# Revit family: EZTE-ELECTRIC ENCL BTM
name_source: partatom
category: Mechanical Equipment
revit_build: Autodesk Revit 2018 (Build: 20170223_1515(x64)
units: mm (PartAtom-declared; Revit-internal decimal feet)

## family parameters
Always vertical = Yes
Cut with Voids When Loaded = No
OmniClass Number = 23.75.00.00
OmniClass Title = Climate Control (HVAC)
Part Type = Normal
Room Calculation Point = No
Round Connector Dimension = Use Diameter
Shared = No
Work Plane-Based = No

## types (9) — shared parameters
Discharge = 0' - 0 5/8"
EZTE Length = 3' - 3 1/2"
EZTE Rear Side = 3' - 2 7/8"
Electric Encl Length = 2' - 0"
Electric Encl distance from discharge = 0' - 2 1/8"
Enclosure Distance from Front = 0' - 4"
Enclosure Height = 0' - 11 3/32"
Enclosure Length = 1' - 2 7/32"
Enclosure Optional = Yes
Inlet Distance S = 0' - 5 3/8"
Width = 0' - 7 1/4"

## per-type parameters (varying)
| type | Between Encl and Electric | DisCharge Height | DisCharge Width | EZTE Height | EZTE Width | Electric Encl E Dimension | Inlet Diameter | Inlet Radius |
| Inlet Size 06 With Controller | 0' - 0 7/16" | 0' - 8 3/4" | 0' - 8 3/4" | 0' - 10" | 0' - 10" | 1' - 0" | 0' - 5 7/8" | 0' - 2 15/16" |
| Inlet Size 05 With Controller | 0' - 0 7/16" | 0' - 8 3/4" | 0' - 8 3/4" | 0' - 10" | 0' - 10" | 1' - 0" | 0' - 4 7/8" | 0' - 2 7/16" |
| Inlet Size 07 With Controller | 0' - 0 7/16" | 0' - 8 3/4" | 0' - 10 3/4" | 0' - 10" | 1' - 0" | 1' - 0" | 0' - 6 7/8" | 0' - 3 7/16" |
| Inlet Size 08 With Controller | 0' - 0 7/16" | 0' - 8 3/4" | 0' - 10 3/4" | 0' - 10" | 1' - 0" | 1' - 0" | 0' - 7 7/8" | 0' - 3 15/16" |
| Inlet Size 09 With Controller | 0' - 0 11/16" | 0' - 11 1/4" | 1' - 0 3/4" | 1' - 0 1/2" | 1' - 2" | 1' - 0 1/2" | 0' - 8 7/8" | 0' - 4 7/16" |
| Inlet Size 10 With Controller | 0' - 0 11/16" | 0' - 11 1/4" | 1' - 0 3/4" | 1' - 0 1/2" | 1' - 2" | 1' - 0 1/2" | 0' - 9 7/8" | 0' - 4 15/16" |
| Inlet Size 12 With Controller | 0' - 1 31/32" | 1' - 1 3/4" | 1' - 2 3/4" | 1' - 3" | 1' - 4" | 1' - 3" | 0' - 11 7/8" | 0' - 5 15/16" |
| Inlet Size 14 With Controller | 0' - 3 7/32" | 1' - 4 1/4" | 1' - 6 3/4" | 1' - 5 1/2" | 1' - 8" | 1' - 5 1/2" | 1' - 1 7/8" | 0' - 6 15/16" |
| Inlet Size 16 With Controller | 0' - 3 7/32" | 1' - 4 1/4" | 1' - 10 3/4" | 1' - 5 1/2" | 2' - 0" | 1' - 5 1/2" | 1' - 2 7/8" | 0' - 7 7/16" |

## geometry (parser evidence)
native form markers: Sweep x5
no freeform markers — native parametric forms only
